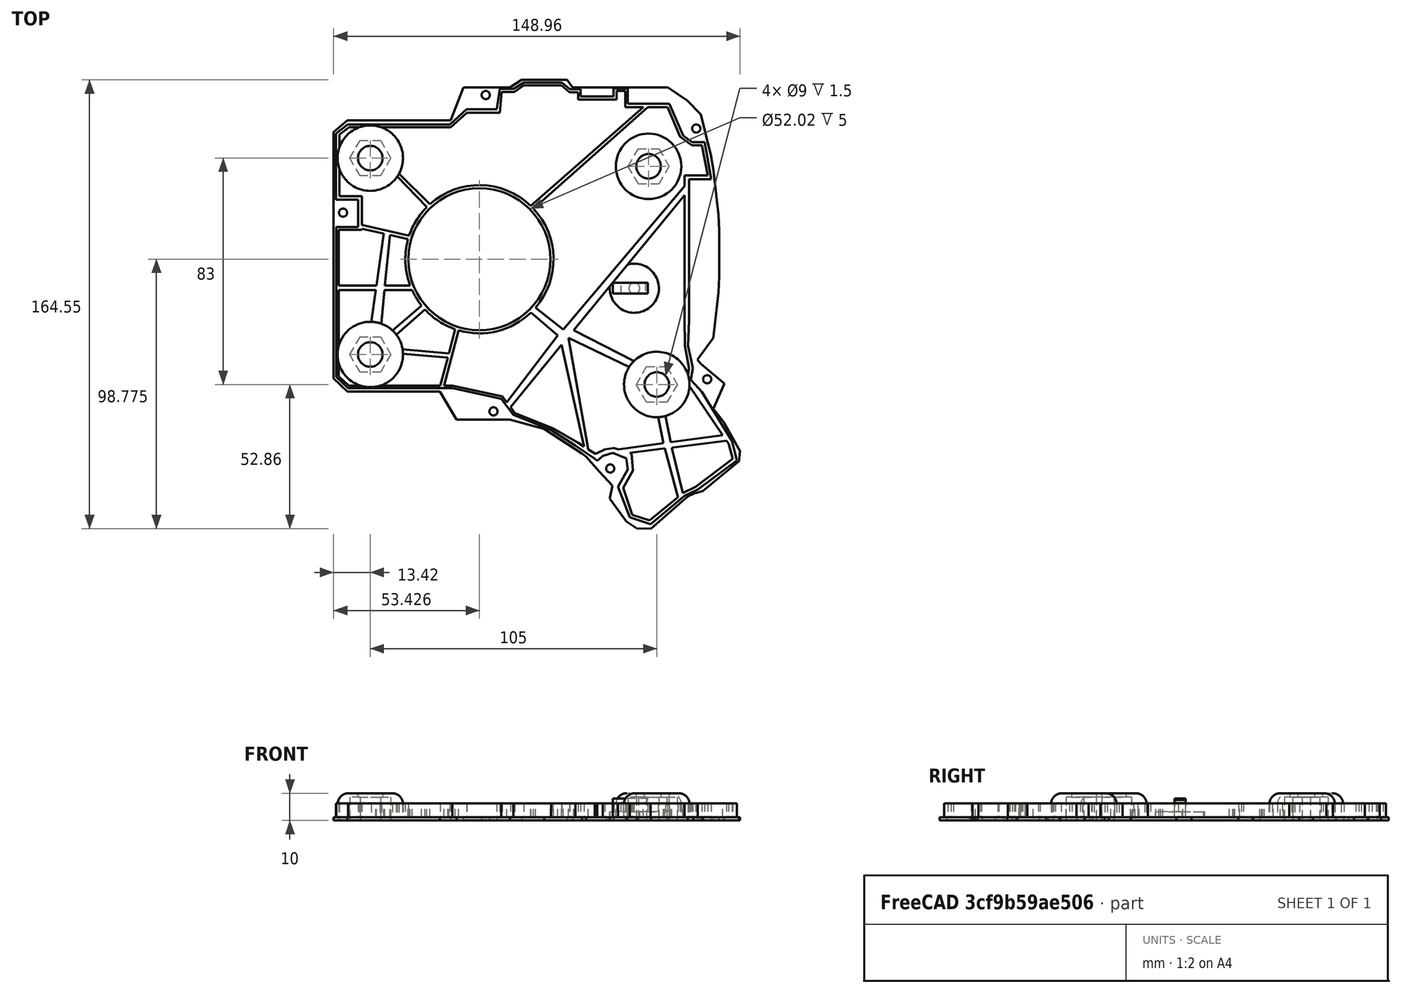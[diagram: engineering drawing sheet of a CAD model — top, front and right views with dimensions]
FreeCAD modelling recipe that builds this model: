
FCSTD DOCUMENT  (FreeCAD 0.19R14555 (Git shallow))
Label: bottom_left
License: All rights reserved
LicenseURL: http://en.wikipedia.org/wiki/All_rights_reserved
objects: Part::Extrusion×13, Sketcher::SketchObject×9, Part::Cut×7, Part::MultiFuse×2, Mesh::Feature×2, Part::Fillet×1, Part::Mirroring×1
note: 33 computed .brp shape members not serialized (recipe doc carries the construction recipe); baked Part::Feature solids carry a one-line shape summary decoded from their .brp

FEATURE [Sketcher::SketchObject] Sketch
  FullyConstrained = false
  Placement = pos=(0,0,0) rot=(1,0,0;1.5708rad)
  sketch-geometry (7):
    g0: LineSegment StartX=-26.8806 StartY=-4.41101 StartZ=0 EndX=-26.8806 EndY=-0.870948 EndZ=0
    g1: LineSegment StartX=-26.8806 StartY=-0.870948 StartZ=0 EndX=-35.8327 EndY=-0.870948 EndZ=0
    g2: LineSegment StartX=-35.8327 StartY=-0.870948 StartZ=0 EndX=-36.775 EndY=0.249898 EndZ=0
    g3: LineSegment StartX=-36.775 StartY=0.249898 StartZ=0 EndX=-36.775 EndY=0.77812 EndZ=0
    g4: LineSegment StartX=-36.775 StartY=0.77812 StartZ=0 EndX=-23.8806 EndY=0.77812 EndZ=0
    g5: LineSegment StartX=-23.8806 StartY=0.77812 StartZ=0 EndX=-23.8806 EndY=-4.41101 EndZ=0
    g6: LineSegment StartX=-23.8806 StartY=-4.41101 StartZ=0 EndX=-26.8806 EndY=-4.41101 EndZ=0
  constraints (14):
    c: Vertical(g0)
    c: Coincident(g0,g1)
    c: Horizontal(g1)
    c: Coincident(g1,g2)
    c: Coincident(g2,g3)
    c: Vertical(g3)
    c: Coincident(g3,g4)
    c: Horizontal(g4)
    c: Coincident(g4,g5)
    c: Vertical(g5)
    c: Coincident(g6,g5)
    c: Coincident(g6,g0)
    c: Horizontal(g6)
    c: Distance(g6) = 3
FEATURE [Part::Extrusion] Extrude  label="Schalterhalter"
  Base = -> Sketch
  Dir = (0,-1,2e-16)
  DirMode = 2
  FaceMakerClass = Part::FaceMakerBullseye
  LengthFwd = 4
  LengthRev = 0
  Placement = pos=(0,-10.7,0) rot=(0,0,1;0rad)
  Solid = true
  Symmetric = false
FEATURE [Sketcher::SketchObject] Sketch031
  FullyConstrained = false
  Placement = pos=(0,0,0) rot=(1,0,0;3.14159rad)
  sketch-geometry (102):
    g0: LineSegment StartX=-24.1385 StartY=-60.4779 StartZ=0 EndX=-29.3451 EndY=-60.4779 EndZ=0
    g1: LineSegment StartX=-29.3451 StartY=-60.4779 StartZ=0 EndX=-29.3451 EndY=-54.9411 EndZ=0
    g2: LineSegment StartX=-29.3451 StartY=-54.9411 StartZ=0 EndX=-44.617 EndY=-54.9411 EndZ=0
    g3: LineSegment StartX=-44.617 StartY=-54.9411 StartZ=0 EndX=-49.6427 EndY=-43.3137 EndZ=0
    g4: LineSegment StartX=-49.6427 StartY=-43.3137 StartZ=0 EndX=-52.9932 EndY=-40.8008 EndZ=0
    g5: LineSegment StartX=-52.9932 StartY=-40.8008 StartZ=0 EndX=-57.5179 EndY=-40.8008 EndZ=0
    g6: LineSegment StartX=-57.5179 StartY=-40.8008 StartZ=0 EndX=-59.9469 EndY=-27.3014 EndZ=0
    g7: LineSegment StartX=-59.9469 StartY=-27.3014 StartZ=0 EndX=-51.7705 EndY=-27.3014 EndZ=0
    g8: LineSegment StartX=-51.7705 StartY=-27.3014 StartZ=0 EndX=-51.7705 EndY=24.5767 EndZ=0
    g9: LineSegment StartX=-51.7705 StartY=24.5767 StartZ=0 EndX=-51.4821 EndY=33.7697 EndZ=0
    g10: LineSegment StartX=-51.4821 StartY=33.7697 StartZ=0 EndX=-53.2529 EndY=41.8955 EndZ=0
    g11: LineSegment StartX=-53.2529 StartY=41.8955 StartZ=0 EndX=-52.4621 EndY=46.2446 EndZ=0
    g12: LineSegment StartX=-52.4621 StartY=46.2446 StartZ=0 EndX=-56.5226 EndY=50.7262 EndZ=0
    g13: LineSegment StartX=-56.5226 StartY=50.7262 StartZ=0 EndX=-67.5901 EndY=68.7223 EndZ=0
    g14: LineSegment StartX=-67.5901 StartY=68.7223 StartZ=0 EndX=-69.3913 EndY=75.8391 EndZ=0
    g15: LineSegment StartX=-69.3913 StartY=75.8391 StartZ=0 EndX=-55.0632 EndY=86.5815 EndZ=0
    g16: LineSegment StartX=-55.0632 StartY=86.5815 StartZ=0 EndX=-50.1429 EndY=88.8659 EndZ=0
    g17: LineSegment StartX=-50.1429 StartY=88.8659 StartZ=0 EndX=-37.7005 EndY=99.2232 EndZ=0
    g18: LineSegment StartX=-37.7005 StartY=99.2232 StartZ=0 EndX=-30.1005 EndY=96.7191 EndZ=0
    g19: LineSegment StartX=-30.1005 StartY=96.7191 StartZ=0 EndX=-25.7646 EndY=85.523 EndZ=0
    g20: LineSegment StartX=-17.2707 StartY=75.2106 StartZ=0 EndX=-10.1077 EndY=70.3434 EndZ=0
    g21: LineSegment StartX=-10.1077 StartY=70.3434 StartZ=0 EndX=-1.25529 EndY=64.7175 EndZ=0
    g22: LineSegment StartX=-1.25529 StartY=64.7175 StartZ=0 EndX=12.6151 EndY=59.0944 EndZ=0
    g23: LineSegment StartX=12.6151 StartY=59.0944 StartZ=0 EndX=16.9593 EndY=53.2146 EndZ=0
    g24: LineSegment StartX=16.9593 StartY=53.2146 StartZ=0 EndX=34.8576 EndY=49.3476 EndZ=0
    g25: LineSegment StartX=34.8576 StartY=49.3476 StartZ=0 EndX=73.1246 EndY=49.3476 EndZ=0
    g26: LineSegment StartX=73.1246 StartY=49.3476 StartZ=0 EndX=77.4982 EndY=45.2021 EndZ=0
    g27: LineSegment StartX=77.4982 StartY=45.2021 StartZ=0 EndX=77.4982 EndY=-9.69727 EndZ=0
    g28: LineSegment StartX=77.4982 StartY=-9.69727 StartZ=0 EndX=69.5024 EndY=-9.69727 EndZ=0
    g29: LineSegment StartX=69.5024 StartY=-9.69727 StartZ=0 EndX=69.5024 EndY=-19.8189 EndZ=0
    g30: LineSegment StartX=69.5024 StartY=-19.8189 StartZ=0 EndX=77.6247 EndY=-19.8189 EndZ=0
    g31: LineSegment StartX=77.6247 StartY=-19.8189 StartZ=0 EndX=77.6247 EndY=-44.0607 EndZ=0
    g32: LineSegment StartX=77.6247 StartY=-44.0607 StartZ=0 EndX=73.2508 EndY=-47.3458 EndZ=0
    g33: LineSegment StartX=73.2508 StartY=-47.3458 StartZ=0 EndX=35.7634 EndY=-47.3458 EndZ=0
    g34: LineSegment StartX=35.7634 StartY=-47.3458 StartZ=0 EndX=29.7437 EndY=-52.8546 EndZ=0
    g35: LineSegment StartX=29.7437 StartY=-52.8546 StartZ=0 EndX=18.6224 EndY=-52.8546 EndZ=0
    g36: LineSegment StartX=18.6224 StartY=-52.8546 StartZ=0 EndX=17.5482 EndY=-60.3492 EndZ=0
    g37: LineSegment StartX=17.5482 StartY=-60.3492 StartZ=0 EndX=12.4995 EndY=-60.3492 EndZ=0
    g38: LineSegment StartX=12.4995 StartY=-60.3492 StartZ=0 EndX=8.72547 EndY=-62.7272 EndZ=0
    g39: LineSegment StartX=8.72547 StartY=-62.7272 StartZ=0 EndX=-5.26983 EndY=-62.7272 EndZ=0
    g40: LineSegment StartX=-5.26983 StartY=-62.7272 StartZ=0 EndX=-8.14386 EndY=-60.228 EndZ=0
    g41: LineSegment StartX=-8.14386 StartY=-60.228 StartZ=0 EndX=-12.0176 EndY=-60.228 EndZ=0
    g42: LineSegment StartX=-12.0176 StartY=-60.228 StartZ=0 EndX=-12.0176 EndY=-57.6039 EndZ=0
    g43: LineSegment StartX=-12.0176 StartY=-57.6039 StartZ=0 EndX=-24.1385 EndY=-57.6039 EndZ=0
    g44: LineSegment StartX=-24.1385 StartY=-57.6039 StartZ=0 EndX=-24.1385 EndY=-60.4779 EndZ=0
    g45: LineSegment StartX=16.9355 StartY=-59.2429 StartZ=0 EndX=12.193 EndY=-59.2429 EndZ=0
    g46: LineSegment StartX=12.193 StartY=-59.2429 StartZ=0 EndX=8.68721 EndY=-61.703 EndZ=0
    g47: LineSegment StartX=8.68721 StartY=-61.703 StartZ=0 EndX=-5.1157 EndY=-61.703 EndZ=0
    g48: LineSegment StartX=-5.1157 StartY=-61.703 StartZ=0 EndX=-8.06111 EndY=-59.199 EndZ=0
    g49: LineSegment StartX=-8.06111 StartY=-59.199 StartZ=0 EndX=-11.1342 EndY=-59.199 EndZ=0
    g50: LineSegment StartX=-11.1342 StartY=-59.199 StartZ=0 EndX=-11.1342 EndY=-56.4281 EndZ=0
    g51: LineSegment StartX=-11.1342 StartY=-56.4281 StartZ=0 EndX=-25.2534 EndY=-56.4281 EndZ=0
    g52: LineSegment StartX=-25.2534 StartY=-56.4281 StartZ=0 EndX=-25.2534 EndY=-59.5911 EndZ=0
    g53: LineSegment StartX=-25.2534 StartY=-59.5911 StartZ=0 EndX=-28.5042 EndY=-59.5911 EndZ=0
    g54: LineSegment StartX=-28.5042 StartY=-59.5911 StartZ=0 EndX=-28.5042 EndY=-53.7043 EndZ=0
    g55: LineSegment StartX=-28.5042 StartY=-53.7043 StartZ=0 EndX=-43.924 EndY=-53.7043 EndZ=0
    g56: LineSegment StartX=-43.924 StartY=-53.7043 StartZ=0 EndX=-48.5049 EndY=-42.8877 EndZ=0
    g57: LineSegment StartX=-48.5049 StartY=-42.8877 StartZ=0 EndX=-52.8786 EndY=-39.7686 EndZ=0
    g58: LineSegment StartX=-52.8786 StartY=-39.7686 StartZ=0 EndX=-56.5882 EndY=-39.7686 EndZ=0
    g59: LineSegment StartX=-56.5882 StartY=-39.7686 StartZ=0 EndX=-58.6529 EndY=-28.6102 EndZ=0
    g60: LineSegment StartX=-58.6529 StartY=-28.6102 StartZ=0 EndX=-50.1741 EndY=-28.6102 EndZ=0
    g61: LineSegment StartX=-50.1741 StartY=-28.6102 StartZ=0 EndX=-50.1741 EndY=23.5651 EndZ=0
    g62: LineSegment StartX=-50.1741 StartY=23.5651 StartZ=0 EndX=-50.3095 EndY=33.8562 EndZ=0
    g63: LineSegment StartX=-50.3095 StartY=33.8562 StartZ=0 EndX=-51.8031 EndY=42.0273 EndZ=0
    g64: LineSegment StartX=-51.8031 StartY=42.0273 StartZ=0 EndX=-50.9245 EndY=46.9475 EndZ=0
    g65: LineSegment StartX=-50.9245 StartY=46.9475 StartZ=0 EndX=-66.2722 EndY=69.6888 EndZ=0
    g66: LineSegment StartX=-66.2722 StartY=69.6888 StartZ=0 EndX=-67.8031 EndY=75.2474 EndZ=0
    g67: LineSegment StartX=-67.8031 StartY=75.2474 StartZ=0 EndX=-54.2724 EndY=85.4832 EndZ=0
    g68: LineSegment StartX=-54.2724 StartY=85.4832 StartZ=0 EndX=-49.5718 EndY=87.8555 EndZ=0
    g69: LineSegment StartX=-49.5718 StartY=87.8555 StartZ=0 EndX=-37.403 EndY=97.7838 EndZ=0
    g70: LineSegment StartX=-37.403 StartY=97.7838 StartZ=0 EndX=-30.9452 EndY=95.8509 EndZ=0
    g71: LineSegment StartX=-30.9452 StartY=95.8509 StartZ=0 EndX=-27.7256 EndY=85.9358 EndZ=0
    g72: LineSegment StartX=-17.5596 StartY=73.4993 StartZ=0 EndX=-11.2059 EndY=69.3769 EndZ=0
    g73: LineSegment StartX=-11.2059 StartY=69.3769 StartZ=0 EndX=-1.89314 EndY=64.0587 EndZ=0
    g74: LineSegment StartX=-1.89314 StartY=64.0587 StartZ=0 EndX=12.006 EndY=58.4019 EndZ=0
    g75: LineSegment StartX=12.006 StartY=58.4019 StartZ=0 EndX=16.5662 EndY=52.3162 EndZ=0
    g76: LineSegment StartX=16.5662 StartY=52.3162 StartZ=0 EndX=34.9016 EndY=48.4585 EndZ=0
    g77: LineSegment StartX=34.9016 StartY=48.4585 StartZ=0 EndX=72.868 EndY=48.4585 EndZ=0
    g78: LineSegment StartX=72.868 StartY=48.4585 StartZ=0 EndX=76.5288 EndY=44.9389 EndZ=0
    g79: LineSegment StartX=76.5288 StartY=44.9389 StartZ=0 EndX=76.5288 EndY=-8.70233 EndZ=0
    g80: LineSegment StartX=76.5288 StartY=-8.70233 StartZ=0 EndX=68.0803 EndY=-8.70233 EndZ=0
    g81: LineSegment StartX=68.0803 StartY=-8.70233 StartZ=0 EndX=68.0803 EndY=-21.0197 EndZ=0
    g82: LineSegment StartX=68.0803 StartY=-21.0197 StartZ=0 EndX=76.3385 EndY=-21.0197 EndZ=0
    g83: LineSegment StartX=76.3385 StartY=-21.0197 StartZ=0 EndX=76.3385 EndY=-43.5888 EndZ=0
    g84: LineSegment StartX=76.3385 StartY=-43.5888 StartZ=0 EndX=72.8241 EndY=-46.2686 EndZ=0
    g85: LineSegment StartX=72.8241 StartY=-46.2686 StartZ=0 EndX=35.499 EndY=-46.2686 EndZ=0
    g86: LineSegment StartX=35.499 StartY=-46.2686 StartZ=0 EndX=29.59 EndY=-51.5989 EndZ=0
    g87: LineSegment StartX=29.59 StartY=-51.5989 StartZ=0 EndX=17.5526 EndY=-51.5989 EndZ=0
    g88: LineSegment StartX=17.5526 StartY=-51.5989 StartZ=0 EndX=16.9355 EndY=-59.2429 EndZ=0
    g89: Circle CenterX=24.994 CenterY=2.08531 CenterZ=0 NormalX=0 NormalY=0 NormalZ=1 AngleXU=0 Radius=26.0078
    g90: Circle CenterX=24.994 CenterY=2.08531 CenterZ=0 NormalX=0 NormalY=0 NormalZ=1 AngleXU=0 Radius=27.1592
    g91: LineSegment StartX=-25.7646 StartY=85.523 StartZ=0 EndX=-29.3769 EndY=79.1757 EndZ=0
    g92: LineSegment StartX=-29.3769 StartY=79.1757 StartZ=0 EndX=-28.8093 EndY=75.1506 EndZ=0
    g93: LineSegment StartX=-28.8093 StartY=75.1506 StartZ=0 EndX=-23.9069 EndY=73.0348 EndZ=0
    g94: LineSegment StartX=-23.9069 StartY=73.0348 StartZ=0 EndX=-20.1398 EndY=74.2217 EndZ=0
    g95: LineSegment StartX=-20.1398 StartY=74.2217 StartZ=0 EndX=-18.2305 EndY=75.9247 EndZ=0
    g96: LineSegment StartX=-18.2305 StartY=75.9247 StartZ=0 EndX=-17.2707 EndY=75.2106 EndZ=0
    g97: LineSegment StartX=-17.5596 StartY=73.4993 StartZ=0 EndX=-20.9655 EndY=71.7963 EndZ=0
    g98: LineSegment StartX=-20.9655 StartY=71.7963 StartZ=0 EndX=-24.2165 EndY=71.2287 EndZ=0
    g99: LineSegment StartX=-24.2165 StartY=71.2287 StartZ=0 EndX=-30.7702 EndY=73.2412 EndZ=0
    g100: LineSegment StartX=-30.7702 StartY=73.2412 StartZ=0 EndX=-31.2863 EndY=79.5369 EndZ=0
    g101: LineSegment StartX=-31.2863 StartY=79.5369 StartZ=0 EndX=-27.7256 EndY=85.9358 EndZ=0
  constraints (141):
    c: Horizontal(g0)
    c: Coincident(g0,g1)
    c: Vertical(g1)
    c: Coincident(g1,g2)
    c: Horizontal(g2)
    c: Coincident(g2,g3)
    c: Coincident(g3,g4)
    c: Coincident(g4,g5)
    c: Horizontal(g5)
    c: Coincident(g5,g6)
    c: Coincident(g6,g7)
    c: Horizontal(g7)
    c: Coincident(g7,g8)
    c: Vertical(g8)
    c: Coincident(g8,g9)
    c: Coincident(g9,g10)
    c: Coincident(g10,g11)
    c: Coincident(g11,g12)
    c: Coincident(g12,g13)
    c: Coincident(g13,g14)
    c: Coincident(g14,g15)
    c: Coincident(g15,g16)
    c: Coincident(g16,g17)
    c: Coincident(g17,g18)
    c: Coincident(g18,g19)
    c: Coincident(g20,g21)
    c: Coincident(g21,g22)
    c: Coincident(g22,g23)
    c: Coincident(g23,g24)
    c: Coincident(g24,g25)
    c: Horizontal(g25)
    c: Coincident(g25,g26)
    c: Coincident(g26,g27)
    c: Vertical(g27)
    c: Coincident(g27,g28)
    c: Horizontal(g28)
    c: Coincident(g28,g29)
    c: Vertical(g29)
    c: Coincident(g29,g30)
    c: Horizontal(g30)
    c: Coincident(g30,g31)
    c: Vertical(g31)
    c: Coincident(g31,g32)
    c: Coincident(g32,g33)
    c: Horizontal(g33)
    c: Coincident(g33,g34)
    c: Coincident(g34,g35)
    c: Horizontal(g35)
    c: Coincident(g35,g36)
    c: Coincident(g36,g37)
    c: Horizontal(g37)
    c: Coincident(g37,g38)
    c: Coincident(g38,g39)
    c: Horizontal(g39)
    c: Coincident(g39,g40)
    c: Coincident(g40,g41)
    c: Horizontal(g41)
    c: Coincident(g41,g42)
    c: Vertical(g42)
    c: Coincident(g42,g43)
    c: Horizontal(g43)
    c: Coincident(g43,g44)
    c: Coincident(g44,g0)
    c: Vertical(g44)
    c: Horizontal(g45)
    c: Coincident(g45,g46)
    c: Coincident(g46,g47)
    c: Horizontal(g47)
    c: Coincident(g47,g48)
    c: Coincident(g48,g49)
    c: Horizontal(g49)
    c: Coincident(g49,g50)
    c: Vertical(g50)
    c: Coincident(g50,g51)
    c: Horizontal(g51)
    c: Coincident(g51,g52)
    c: Vertical(g52)
    c: Coincident(g52,g53)
    c: Horizontal(g53)
    c: Coincident(g53,g54)
    c: Vertical(g54)
    c: Coincident(g54,g55)
    c: Horizontal(g55)
    c: Coincident(g55,g56)
    c: Coincident(g56,g57)
    c: Coincident(g57,g58)
    c: Horizontal(g58)
    c: Coincident(g58,g59)
    c: Coincident(g59,g60)
    c: Horizontal(g60)
    c: Coincident(g60,g61)
    c: Vertical(g61)
    c: Coincident(g61,g62)
    c: Coincident(g62,g63)
    c: Coincident(g63,g64)
    c: Coincident(g64,g65)
    c: Coincident(g65,g66)
    c: Coincident(g66,g67)
    c: Coincident(g67,g68)
    c: Coincident(g68,g69)
    c: Coincident(g69,g70)
    c: Coincident(g70,g71)
    c: Coincident(g72,g73)
    c: Coincident(g73,g74)
    c: Coincident(g74,g75)
    c: Coincident(g75,g76)
    c: Coincident(g76,g77)
    c: Horizontal(g77)
    c: Coincident(g77,g78)
    c: Coincident(g78,g79)
    c: Vertical(g79)
    c: Coincident(g79,g80)
    c: Horizontal(g80)
    c: Coincident(g80,g81)
    c: Vertical(g81)
    c: Coincident(g81,g82)
    c: Horizontal(g82)
    c: Coincident(g82,g83)
    c: Vertical(g83)
    c: Coincident(g83,g84)
    c: Coincident(g84,g85)
    c: Horizontal(g85)
    c: Coincident(g85,g86)
    c: Coincident(g86,g87)
    c: Horizontal(g87)
    c: Coincident(g87,g88)
    c: Coincident(g88,g45)
    c: Coincident(g90,g89)
    c: Coincident(g91,g19)
    c: Coincident(g92,g91)
    c: Coincident(g93,g92)
    c: Coincident(g94,g93)
    c: Coincident(g95,g94)
    c: Coincident(g96,g95)
    c: Coincident(g96,g20)
    c: Coincident(g97,g72)
    c: Coincident(g98,g97)
    c: Coincident(g99,g98)
    c: Coincident(g100,g99)
    c: Coincident(g101,g100)
    c: Coincident(g101,g71)
FEATURE [Part::Extrusion] Extrude026
  Base = -> Sketch031
  Dir = (0,0,-1)
  DirMode = 2
  FaceMakerClass = Part::FaceMakerBullseye
  LengthFwd = 5
  LengthRev = 0
  Placement = pos=(0,0,-1) rot=(0,0,1;0rad)
  Solid = true
  Symmetric = false
FEATURE [Sketcher::SketchObject] Sketch032
  FullyConstrained = false
  sketch-geometry (63):
    g0: LineSegment StartX=-32.5769 StartY=-39.9295 StartZ=0 EndX=-9.54298 EndY=-28.1078 EndZ=0
    g1: LineSegment StartX=-30.7152 StartY=-41.9456 StartZ=0 EndX=-32.5769 EndY=-39.9295 EndZ=0
    g2: LineSegment StartX=32.5107 StartY=-27.5505 StartZ=0 EndX=38.0602 EndY=-48.9351 EndZ=0
    g3: LineSegment StartX=38.0602 StartY=-48.9351 StartZ=0 EndX=39.3736 EndY=-48.6733 EndZ=0
    g4: LineSegment StartX=39.3736 StartY=-48.6733 StartZ=0 EndX=36.6148 EndY=-38.1783 EndZ=0
    g5: LineSegment StartX=33.7238 StartY=-27.1808 StartZ=0 EndX=32.5107 EndY=-27.5505 EndZ=0
    g6: LineSegment StartX=50.4968 StartY=5.20014 StartZ=0 EndX=57.8214 EndY=6.84598 EndZ=0
    g7: LineSegment StartX=69.1965 StartY=9.40202 StartZ=0 EndX=69.1965 EndY=10.7361 EndZ=0
    g8: LineSegment StartX=69.1965 StartY=10.7361 StartZ=0 EndX=49.9077 EndY=6.36256 EndZ=0
    g9: LineSegment StartX=49.9077 StartY=6.36256 StartZ=0 EndX=50.4968 EndY=5.20014 EndZ=0
    g10: LineSegment StartX=6.85712 StartY=16.9685 StartZ=0 EndX=-36.1659 EndY=54.6592 EndZ=0
    g11: LineSegment StartX=-36.1659 StartY=54.6592 StartZ=0 EndX=-37.7589 EndY=54.5817 EndZ=0
    g12: LineSegment StartX=-37.7589 StartY=54.5817 StartZ=0 EndX=5.83785 EndY=15.8428 EndZ=0
    g13: LineSegment StartX=5.83785 StartY=15.8428 StartZ=0 EndX=6.85712 EndY=16.9685 EndZ=0
    g14: LineSegment StartX=-30.7152 StartY=-41.9456 StartZ=0 EndX=-7.65656 EndY=-30.8878 EndZ=0
    g15: LineSegment StartX=-15.0169 StartY=-72.5869 StartZ=0 EndX=-13.4959 EndY=-71.5729 EndZ=0
    g16: LineSegment StartX=-13.4959 StartY=-71.5729 StartZ=0 EndX=-5.11632 EndY=-33.503 EndZ=0
    g17: LineSegment StartX=44.4369 StartY=-20.0606 StartZ=0 EndX=56.2289 EndY=-30.3786 EndZ=0
    g18: LineSegment StartX=56.2289 StartY=-30.3786 StartZ=0 EndX=57.3297 EndY=-28.5909 EndZ=0
    g19: LineSegment StartX=57.3297 StartY=-28.5909 StartZ=0 EndX=45.6345 EndY=-18.5823 EndZ=0
    g20: LineSegment StartX=45.6345 StartY=-18.5823 StartZ=0 EndX=44.4369 EndY=-20.0606 EndZ=0
    g21: LineSegment StartX=55.0145 StartY=29.918 StartZ=0 EndX=42.7023 EndY=17.6926 EndZ=0
    g22: LineSegment StartX=42.7023 StartY=17.6926 StartZ=0 EndX=43.6798 EndY=16.4587 EndZ=0
    g23: LineSegment StartX=43.6798 StartY=16.4587 StartZ=0 EndX=55.8612 EndY=29.0011 EndZ=0
    g24: LineSegment StartX=55.8612 StartY=29.0011 StartZ=0 EndX=55.0145 EndY=29.918 EndZ=0
    g25: LineSegment StartX=36.2165 StartY=-36.6632 StartZ=0 EndX=53.7558 EndY=-34.9819 EndZ=0
    g26: LineSegment StartX=53.7558 StartY=-34.9819 StartZ=0 EndX=53.3152 EndY=-36.7098 EndZ=0
    g27: LineSegment StartX=53.3152 StartY=-36.7098 StartZ=0 EndX=36.6148 EndY=-38.1783 EndZ=0
    g28: LineSegment StartX=36.2165 StartY=-36.6632 StartZ=0 EndX=33.7238 EndY=-27.1808 EndZ=0
    g29: LineSegment StartX=57.8214 StartY=6.84598 StartZ=0 EndX=59.6195 EndY=-11.7601 EndZ=0
    g30: LineSegment StartX=60.9963 StartY=-26.0063 StartZ=0 EndX=64.7176 EndY=-25.5862 EndZ=0
    g31: LineSegment StartX=64.7176 StartY=-25.5862 StartZ=0 EndX=62.9989 EndY=-13.4017 EndZ=0
    g32: LineSegment StartX=60.0714 StartY=7.35159 StartZ=0 EndX=69.1965 EndY=9.40202 EndZ=0
    g33: LineSegment StartX=-49.6869 StartY=-88.2689 StartZ=0 EndX=-47.9566 EndY=-89.9327 EndZ=0
    g34: LineSegment StartX=-47.9566 StartY=-89.9327 StartZ=0 EndX=-42.9299 EndY=-71.4391 EndZ=0
    g35: LineSegment StartX=62.7673 StartY=-11.7601 StartZ=0 EndX=77.2056 EndY=-11.7601 EndZ=0
    g36: LineSegment StartX=77.2056 StartY=-11.7601 StartZ=0 EndX=77.2056 EndY=-13.4017 EndZ=0
    g37: LineSegment StartX=77.2056 StartY=-13.4017 StartZ=0 EndX=62.9989 EndY=-13.4017 EndZ=0
    g38: LineSegment StartX=59.7782 StartY=-13.4017 StartZ=0 EndX=48.6753 EndY=-13.4017 EndZ=0
    g39: LineSegment StartX=48.6753 StartY=-13.4017 StartZ=0 EndX=49.3718 EndY=-11.7601 EndZ=0
    g40: LineSegment StartX=49.3718 StartY=-11.7601 StartZ=0 EndX=59.6195 EndY=-11.7601 EndZ=0
    g41: LineSegment StartX=59.7782 StartY=-13.4017 StartZ=0 EndX=60.9963 EndY=-26.0063 EndZ=0
    g42: LineSegment StartX=62.7673 StartY=-11.7601 StartZ=0 EndX=60.0714 EndY=7.35159 EndZ=0
    g43: LineSegment StartX=-65.0366 StartY=-66.5004 StartZ=0 EndX=-66.1967 EndY=-68.5189 EndZ=0
    g44: LineSegment StartX=-66.1967 StartY=-68.5189 StartZ=0 EndX=-45.4188 EndY=-71.1267 EndZ=0
    g45: LineSegment StartX=-25.7061 StartY=-73.6009 StartZ=0 EndX=-24.4808 EndY=-71.9531 EndZ=0
    g46: LineSegment StartX=-24.4808 StartY=-71.9531 StartZ=0 EndX=-42.4246 EndY=-69.5406 EndZ=0
    g47: LineSegment StartX=-45.4188 StartY=-71.1267 StartZ=0 EndX=-49.6869 EndY=-88.2689 EndZ=0
    g48: LineSegment StartX=-42.9299 StartY=-71.4391 StartZ=0 EndX=-25.7061 EndY=-73.6009 EndZ=0
    g49: LineSegment StartX=13.9098 StartY=-56.6917 StartZ=0 EndX=-5.11632 EndY=-33.503 EndZ=0
    g50: LineSegment StartX=-51.0941 StartY=22.5342 StartZ=0 EndX=-51.0941 EndY=25.8134 EndZ=0
    g51: LineSegment StartX=-51.0941 StartY=25.8134 StartZ=0 EndX=-5.73278 EndY=-27.8323 EndZ=0
    g52: LineSegment StartX=15.1277 StartY=-54.8099 StartZ=0 EndX=13.9098 EndY=-56.6917 EndZ=0
    g53: LineSegment StartX=-7.65656 StartY=-30.8878 StartZ=0 EndX=-15.0169 EndY=-72.5869 EndZ=0
    g54: LineSegment StartX=-9.54298 StartY=-28.1078 StartZ=0 EndX=-51.0941 EndY=22.5342 EndZ=0
    g55: LineSegment StartX=-3.74708 StartY=-30.0166 StartZ=0 EndX=15.1277 EndY=-54.8099 EndZ=0
    g56: LineSegment StartX=-5.73278 StartY=-27.8323 StartZ=0 EndX=4.80151 EndY=-19.6249 EndZ=0
    g57: LineSegment StartX=4.80151 StartY=-19.6249 StartZ=0 EndX=6.47927 EndY=-21.2795 EndZ=0
    g58: LineSegment StartX=6.47927 StartY=-21.2795 StartZ=0 EndX=-3.74708 EndY=-30.0166 EndZ=0
    g59: LineSegment StartX=-45.0759 StartY=-69.1841 StartZ=0 EndX=-42.9979 EndY=-58.5171 EndZ=0
    g60: LineSegment StartX=-42.9979 StartY=-58.5171 StartZ=0 EndX=-40.2766 EndY=-58.8293 EndZ=0
    g61: LineSegment StartX=-40.2766 StartY=-58.8293 StartZ=0 EndX=-42.4246 EndY=-69.5406 EndZ=0
    g62: LineSegment StartX=-45.0759 StartY=-69.1841 StartZ=0 EndX=-65.0366 EndY=-66.5004 EndZ=0
  constraints (78):
    c: Coincident(g1,g0)
    c: Coincident(g2,g3)
    c: Coincident(g3,g4)
    c: Coincident(g28,g5)
    c: Coincident(g5,g2)
    c: Coincident(g32,g7)
    c: Vertical(g7)
    c: Coincident(g7,g8)
    c: Coincident(g8,g9)
    c: Coincident(g9,g6)
    c: Coincident(g11,g12)
    c: Coincident(g12,g13)
    c: Coincident(g13,g10)
    c: Coincident(g53,g15)
    c: Coincident(g15,g16)
    c: Coincident(g17,g18)
    c: Coincident(g18,g19)
    c: Coincident(g19,g20)
    c: Coincident(g20,g17)
    c: Coincident(g21,g22)
    c: Coincident(g22,g23)
    c: Coincident(g23,g24)
    c: Coincident(g24,g21)
    c: Coincident(g26,g25)
    c: Coincident(g4,g27)
    c: Coincident(g28,g25)
    c: Tangent(g4,g28)
    c: Coincident(g41,g30)
    c: Coincident(g30,g31)
    c: Coincident(g6,g29)
    c: Coincident(g32,g42)
    c: Tangent(g6,g32)
    c: Coincident(g47,g33)
    c: Coincident(g33,g34)
    c: Horizontal(g35)
    c: Coincident(g35,g36)
    c: Vertical(g36)
    c: Coincident(g36,g37)
    c: Horizontal(g37)
    c: Horizontal(g38)
    c: Coincident(g38,g39)
    c: Coincident(g39,g40)
    c: Horizontal(g40)
    c: Coincident(g29,g40)
    c: Coincident(g41,g38)
    c: Tangent(g29,g41)
    c: Coincident(g31,g37)
    c: Coincident(g42,g35)
    c: Tangent(g31,g42)
    c: PointOnObject(g31,g38)
    c: PointOnObject(g35,g40)
    c: Coincident(g10,g11)
    c: Coincident(g43,g44)
    c: Coincident(g48,g45)
    c: Coincident(g45,g46)
    c: Coincident(g44,g47)
    c: Coincident(g48,g34)
    c: Tangent(g44,g48)
    c: Coincident(g43,g62)
    c: Coincident(g14,g1)
    c: Coincident(g54,g50)
    c: Vertical(g50)
    c: Coincident(g50,g51)
    c: Coincident(g55,g52)
    c: Coincident(g52,g49)
    c: Coincident(g54,g0)
    c: Tangent(g49,g54)
    c: Coincident(g49,g16)
    c: Coincident(g14,g53)
    c: Coincident(g51,g56)
    c: Coincident(g56,g57)
    c: Coincident(g57,g58)
    c: Coincident(g58,g55)
    c: Coincident(g59,g60)
    c: Coincident(g60,g61)
    c: Coincident(g46,g61)
    c: Coincident(g62,g59)
    c: Tangent(g46,g62)
FEATURE [Part::Extrusion] Extrude028  label="Querstreben"
  Base = -> Sketch032
  Dir = (0,0,1)
  DirMode = 2
  FaceMakerClass = Part::FaceMakerBullseye
  LengthFwd = 5
  LengthRev = 0
  Placement = pos=(0,0,-6) rot=(0,0,1;0rad)
  Solid = true
  Symmetric = false
FEATURE [Sketcher::SketchObject] Sketch054
  FullyConstrained = false
  Placement = pos=(0,0,-4) rot=(1,0,0;3.14159rad)
  sketch-geometry (42):
    g0: LineSegment StartX=-44.1096 StartY=-60.8699 StartZ=0 EndX=-51.1597 EndY=-56.0764 EndZ=0
    g1: LineSegment StartX=-51.1597 StartY=-56.0764 StartZ=0 EndX=-56.1597 EndY=-51.0764 EndZ=0
    g2: LineSegment StartX=-56.1597 StartY=-51.0764 StartZ=0 EndX=-59.8373 EndY=-36.0023 EndZ=0
    g3: LineSegment StartX=-59.8373 StartY=-36.0023 StartZ=0 EndX=-60.7273 EndY=-30.9176 EndZ=0
    g4: LineSegment StartX=-60.7273 StartY=-30.9176 StartZ=0 EndX=-62.6338 EndY=-14.0857 EndZ=0
    g5: LineSegment StartX=-62.6338 StartY=-14.0857 StartZ=0 EndX=-62.9339 EndY=-8.65493 EndZ=0
    g6: LineSegment StartX=-62.9339 StartY=-8.65493 StartZ=0 EndX=-62.9339 EndY=8.50371 EndZ=0
    g7: LineSegment StartX=-62.9339 StartY=8.50371 StartZ=0 EndX=-62.6306 EndY=14.1113 EndZ=0
    g8: LineSegment StartX=-62.6306 StartY=14.1113 StartZ=0 EndX=-60.7274 EndY=30.9184 EndZ=0
    g9: LineSegment StartX=-60.7274 StartY=30.9184 StartZ=0 EndX=-54.9343 EndY=38.937 EndZ=0
    g10: LineSegment StartX=-54.9343 StartY=38.937 StartZ=0 EndX=-56.1902 EndY=40.4684 EndZ=0
    g11: LineSegment StartX=-64.8157 StartY=47.7061 StartZ=0 EndX=-60.7702 EndY=56.9561 EndZ=0
    g12: LineSegment StartX=-60.7702 StartY=56.9561 StartZ=0 EndX=-64.4792 EndY=61.7033 EndZ=0
    g13: LineSegment StartX=-64.4792 StartY=61.7033 StartZ=0 EndX=-70.5416 EndY=72.3745 EndZ=0
    g14: LineSegment StartX=-70.5416 StartY=72.3745 StartZ=0 EndX=-70.1745 EndY=76.1634 EndZ=0
    g15: LineSegment StartX=-70.1745 StartY=76.1634 StartZ=0 EndX=-56.8443 EndY=87.0814 EndZ=0
    g16: LineSegment StartX=-51.3142 StartY=89.1273 StartZ=0 EndX=-37.9034 EndY=100.86 EndZ=0
    g17: LineSegment StartX=-23.7658 StartY=85.1928 StartZ=0 EndX=-18.9923 EndY=79.8913 EndZ=0
    g18: LineSegment StartX=-18.9923 StartY=79.8913 StartZ=0 EndX=-14.1134 EndY=74.4727 EndZ=0
    g19: LineSegment StartX=1.2105 StartY=64.3357 StartZ=0 EndX=13.8377 EndY=60.8699 EndZ=0
    g20: LineSegment StartX=13.8377 StartY=60.8699 StartZ=0 EndX=33.3369 EndY=60.8699 EndZ=0
    g21: LineSegment StartX=33.3369 StartY=60.8699 StartZ=0 EndX=39.4269 EndY=50.5485 EndZ=0
    g22: LineSegment StartX=39.4269 StartY=50.5485 StartZ=0 EndX=73.4211 EndY=50.5485 EndZ=0
    g23: LineSegment StartX=73.4211 StartY=50.5485 StartZ=0 EndX=78.4211 EndY=45.7188 EndZ=0
    g24: LineSegment StartX=78.4211 StartY=45.7188 StartZ=0 EndX=78.4211 EndY=-44.5398 EndZ=0
    g25: LineSegment StartX=78.4211 StartY=-44.5398 StartZ=0 EndX=73.4211 EndY=-48.8699 EndZ=0
    g26: LineSegment StartX=73.4211 StartY=-48.8699 StartZ=0 EndX=35.5981 EndY=-48.8699 EndZ=0
    g27: LineSegment StartX=35.5981 StartY=-48.8699 StartZ=0 EndX=30.8749 EndY=-60.8699 EndZ=0
    g28: LineSegment StartX=30.8749 StartY=-60.8699 StartZ=0 EndX=13.8377 EndY=-60.8699 EndZ=0
    g29: LineSegment StartX=13.8377 StartY=-60.8699 StartZ=0 EndX=9.45978 EndY=-63.6899 EndZ=0
    g30: LineSegment StartX=9.45978 StartY=-63.6899 StartZ=0 EndX=-7.15413 EndY=-63.6899 EndZ=0
    g31: LineSegment StartX=-7.15413 StartY=-63.6899 StartZ=0 EndX=-9.13059 EndY=-60.8699 EndZ=0
    g32: LineSegment StartX=-9.13059 StartY=-60.8699 StartZ=0 EndX=-44.1096 EndY=-60.8699 EndZ=0
    g33: LineSegment StartX=-56.1902 StartY=40.4684 StartZ=0 EndX=-64.8157 EndY=47.7061 EndZ=0
    g34: LineSegment StartX=-56.8443 StartY=87.0814 StartZ=0 EndX=-53.5266 EndY=88.046 EndZ=0
    g35: LineSegment StartX=-53.5266 StartY=88.046 StartZ=0 EndX=-51.3142 EndY=89.1273 EndZ=0
    g36: LineSegment StartX=-28.7993 StartY=98.2142 StartZ=0 EndX=-22.7532 EndY=89.8924 EndZ=0
    g37: LineSegment StartX=-22.7532 StartY=89.8924 StartZ=0 EndX=-23.7658 EndY=85.1928 EndZ=0
    g38: LineSegment StartX=-37.9034 StartY=100.86 StartZ=0 EndX=-32.6869 EndY=100.79 EndZ=0
    g39: LineSegment StartX=-32.6869 StartY=100.79 StartZ=0 EndX=-28.7993 EndY=98.2142 EndZ=0
    g40: LineSegment StartX=-14.1134 StartY=74.4727 StartZ=0 EndX=-12.5391 EndY=73.271 EndZ=0
    g41: LineSegment StartX=-12.5391 StartY=73.271 StartZ=0 EndX=1.2105 EndY=64.3357 EndZ=0
  constraints (50):
    c: Coincident(g0,g1)
    c: Coincident(g1,g2)
    c: Coincident(g2,g3)
    c: Coincident(g3,g4)
    c: Coincident(g4,g5)
    c: Coincident(g5,g6)
    c: Vertical(g6)
    c: Coincident(g6,g7)
    c: Coincident(g7,g8)
    c: Coincident(g8,g9)
    c: Coincident(g9,g10)
    c: Coincident(g11,g12)
    c: Coincident(g12,g13)
    c: Coincident(g13,g14)
    c: Coincident(g14,g15)
    c: Coincident(g17,g18)
    c: Coincident(g19,g20)
    c: Horizontal(g20)
    c: Coincident(g20,g21)
    c: Coincident(g21,g22)
    c: Horizontal(g22)
    c: Coincident(g22,g23)
    c: Coincident(g23,g24)
    c: Vertical(g24)
    c: Coincident(g24,g25)
    c: Coincident(g25,g26)
    c: Horizontal(g26)
    c: Coincident(g26,g27)
    c: Coincident(g27,g28)
    c: Horizontal(g28)
    c: Coincident(g28,g29)
    c: Coincident(g29,g30)
    c: Horizontal(g30)
    c: Coincident(g30,g31)
    c: Coincident(g31,g32)
    c: Horizontal(g32)
    c: Coincident(g0,g32)
    c: Coincident(g33,g11)
    c: Coincident(g34,g15)
    c: Coincident(g35,g34)
    c: Coincident(g35,g16)
    c: Coincident(g37,g36)
    c: Coincident(g37,g17)
    c: Coincident(g10,g33)
    c: Coincident(g16,g38)
    c: Coincident(g38,g39)
    c: Coincident(g39,g36)
    c: Coincident(g40,g18)
    c: Coincident(g41,g40)
    c: Coincident(g41,g19)
FEATURE [Part::Extrusion] Extrude044  label="Grund"
  Base = -> Sketch054
  Dir = (0,0,-1)
  DirMode = 2
  FaceMakerClass = Part::FaceMakerBullseye
  LengthFwd = 1.25
  LengthRev = 0
  Placement = pos=(0,0,-2) rot=(0,0,1;0rad)
  Solid = true
  Symmetric = false
FEATURE [Sketcher::SketchObject] Sketch002
  FullyConstrained = false
  sketch-geometry (7):
    g0: LineSegment StartX=3.75278 StartY=6.5 StartZ=0 EndX=-3.75278 EndY=6.5 EndZ=0
    g1: LineSegment StartX=-3.75278 StartY=6.5 StartZ=0 EndX=-7.50555 EndY=-1.2284e-12 EndZ=0
    g2: LineSegment StartX=-7.50555 StartY=-1.2284e-12 StartZ=0 EndX=-3.75278 EndY=-6.5 EndZ=0
    g3: LineSegment StartX=-3.75278 StartY=-6.5 StartZ=0 EndX=3.75278 EndY=-6.5 EndZ=0
    g4: LineSegment StartX=3.75278 StartY=-6.5 StartZ=0 EndX=7.50555 EndY=6.422e-13 EndZ=0
    g5: LineSegment StartX=7.50555 StartY=6.419e-13 StartZ=0 EndX=3.75278 EndY=6.5 EndZ=0
    g6: Circle CenterX=0 CenterY=0 CenterZ=0 NormalX=0 NormalY=0 NormalZ=1 AngleXU=0 Radius=7.50555
  constraints (16):
    c: Coincident(g0,g1)
    c: Coincident(g1,g2)
    c: Coincident(g2,g3)
    c: Coincident(g3,g4)
    c: Coincident(g4,g5)
    c: Coincident(g5,g0)
    c: Equal(g0, g1-g5) x5
    c: PointOnObject(g0,g6)
    c: PointOnObject(g1,g6)
    c: PointOnObject(g2,g6)
    c: PointOnObject(g3,g6)
    c: PointOnObject(g4,g6)
    c: PointOnObject(g5,g6)
    c: Horizontal(g0)
    c: Distance(g3,g1) = 13
    c: Coincident(g6,g-1)
FEATURE [Part::Extrusion] Extrude002  label="Mutterloch"
  Base = -> Sketch002
  Dir = (0,0,1)
  DirMode = 2
  FaceMakerClass = Part::FaceMakerBullseye
  LengthFwd = 8.5
  LengthRev = 0
  Reversed = true
  Solid = true
  Symmetric = false
FEATURE [Sketcher::SketchObject] Sketch055
  FullyConstrained = false
  sketch-geometry (1):
    g0: Circle CenterX=0 CenterY=0 CenterZ=0 NormalX=0 NormalY=0 NormalZ=1 AngleXU=0 Radius=12
  constraints (2):
    c: Coincident(g0,g-1)
    c: Radius(g0) = 12
FEATURE [Part::Extrusion] Extrude045
  Base = -> Sketch055
  Dir = (0,0,1)
  DirMode = 2
  FaceMakerClass = Part::FaceMakerBullseye
  LengthFwd = 10
  LengthRev = 0
  Placement = pos=(0,0,-8.5) rot=(0,0,1;0rad)
  Solid = true
  Symmetric = false
FEATURE [Part::Fillet] Fillet
  Base = -> Extrude045
  Edges = 1 edges r=4: [Edge3]
FEATURE [Sketcher::SketchObject] Sketch056
  FullyConstrained = false
  sketch-geometry (1):
    g0: Circle CenterX=0 CenterY=0 CenterZ=0 NormalX=0 NormalY=0 NormalZ=1 AngleXU=0 Radius=4.5
  constraints (2):
    c: Coincident(g0,g-1)
    c: Radius(g0) = 4.5
FEATURE [Part::Extrusion] Extrude046
  Base = -> Sketch056
  Dir = (0,0,1)
  DirMode = 2
  FaceMakerClass = Part::FaceMakerBullseye
  LengthFwd = 10
  LengthRev = 0
  Solid = true
  Symmetric = false
FEATURE [Part::Cut] Cut
  Base = -> Fillet
  Tool = -> Extrude046
FEATURE [Part::Cut] Cut001
  Base = -> Cut
  Placement = pos=(65,-37,1.25) rot=(0,0,1;0rad)
  Tool = -> Extrude002
FEATURE [Part::Cut] Cut002
  Base = -> Cut
  Placement = pos=(65,35,1.25) rot=(0,0,1;0rad)
  Tool = -> Extrude002
FEATURE [Part::Cut] Cut003
  Base = -> Cut
  Placement = pos=(-37,32,1.25) rot=(0,0,1;0rad)
  Tool = -> Extrude002
FEATURE [Part::Cut] Cut004
  Base = -> Cut
  Placement = pos=(-40,-48,1.25) rot=(0,0,1;0rad)
  Tool = -> Extrude002
FEATURE [Part::Extrusion] Extrude047  label="Mutterloch001"
  Base = -> Sketch002
  Dir = (0,0,1)
  DirMode = 2
  FaceMakerClass = Part::FaceMakerBullseye
  LengthFwd = 8.5
  LengthRev = 0
  Placement = pos=(65,-37,1.25) rot=(0,0,1;0rad)
  Reversed = true
  Solid = true
  Symmetric = false
FEATURE [Part::Extrusion] Extrude048  label="Mutterloch002"
  Base = -> Sketch002
  Dir = (0,0,1)
  DirMode = 2
  FaceMakerClass = Part::FaceMakerBullseye
  LengthFwd = 8.5
  LengthRev = 0
  Placement = pos=(65,35,1.25) rot=(0,0,1;0rad)
  Reversed = true
  Solid = true
  Symmetric = false
FEATURE [Part::Extrusion] Extrude049  label="Mutterloch003"
  Base = -> Sketch002
  Dir = (0,0,1)
  DirMode = 2
  FaceMakerClass = Part::FaceMakerBullseye
  LengthFwd = 8.5
  LengthRev = 0
  Placement = pos=(-37,32,1.25) rot=(0,0,1;0rad)
  Reversed = true
  Solid = true
  Symmetric = false
FEATURE [Part::Extrusion] Extrude050  label="Mutterloch004"
  Base = -> Sketch002
  Dir = (0,0,1)
  DirMode = 2
  FaceMakerClass = Part::FaceMakerBullseye
  LengthFwd = 8.5
  LengthRev = 0
  Placement = pos=(-40,-48,1.25) rot=(0,0,1;0rad)
  Reversed = true
  Solid = true
  Symmetric = false
FEATURE [Part::MultiFuse] Fusion001
  Shapes = -> [Extrude050,Extrude049,Extrude048,Extrude047]
FEATURE [Part::Cut] Cut005
  Base = -> Extrude044
  Tool = -> Fusion001
FEATURE [Sketcher::SketchObject] Sketch033
  FullyConstrained = false
  Placement = pos=(0,0,0) rot=(1,0,0;3.14159rad)
  sketch-geometry (2):
    g0: Circle CenterX=-31.7644 CenterY=12.7082 CenterZ=0 NormalX=0 NormalY=0 NormalZ=1 AngleXU=0 Radius=2
    g1: Circle CenterX=-31.7644 CenterY=12.7082 CenterZ=0 NormalX=0 NormalY=0 NormalZ=1 AngleXU=0 Radius=9
  constraints (3):
    c: Coincident(g1,g0)
    c: Radius(g0) = 2
    c: Radius(g1) = 9
FEATURE [Part::Extrusion] Extrude029  label="Schalterbasis"
  Base = -> Sketch033
  Dir = (0,0,-1)
  DirMode = 2
  FaceMakerClass = Part::FaceMakerBullseye
  LengthFwd = 2
  LengthRev = 0
  Placement = pos=(0,0,-4) rot=(0,0,1;0rad)
  Solid = true
  Symmetric = false
FEATURE [Sketcher::SketchObject] Sketch057
  FullyConstrained = false
  Placement = pos=(0,0,0) rot=(1,0,0;3.14159rad)
  sketch-geometry (12):
    g0: Circle CenterX=-58.4659 CenterY=46.0837 CenterZ=0 NormalX=0 NormalY=0 NormalZ=1 AngleXU=0 Radius=1.5
    g1: Circle CenterX=-58.4659 CenterY=46.0837 CenterZ=0 NormalX=0 NormalY=0 NormalZ=1 AngleXU=0 Radius=2.64
    g2: Circle CenterX=-22.9147 CenterY=78.8059 CenterZ=0 NormalX=0 NormalY=0 NormalZ=1 AngleXU=0 Radius=1.5
    g3: Circle CenterX=-22.9147 CenterY=78.8059 CenterZ=0 NormalX=0 NormalY=0 NormalZ=1 AngleXU=0 Radius=2.64
    g4: Circle CenterX=19.8371 CenterY=57.8529 CenterZ=0 NormalX=0 NormalY=0 NormalZ=1 AngleXU=0 Radius=1.5
    g5: Circle CenterX=19.8371 CenterY=57.8529 CenterZ=0 NormalX=0 NormalY=0 NormalZ=1 AngleXU=0 Radius=2.64
    g6: Circle CenterX=74.9864 CenterY=-15.0107 CenterZ=0 NormalX=0 NormalY=0 NormalZ=1 AngleXU=0 Radius=1.5
    g7: Circle CenterX=74.9864 CenterY=-15.0107 CenterZ=0 NormalX=0 NormalY=0 NormalZ=1 AngleXU=0 Radius=2.64
    g8: Circle CenterX=22.6987 CenterY=-58.1327 CenterZ=0 NormalX=0 NormalY=0 NormalZ=1 AngleXU=0 Radius=1.5
    g9: Circle CenterX=22.6987 CenterY=-58.1327 CenterZ=0 NormalX=0 NormalY=0 NormalZ=1 AngleXU=0 Radius=2.64
    g10: Circle CenterX=-54.4678 CenterY=-45.841 CenterZ=0 NormalX=0 NormalY=0 NormalZ=1 AngleXU=0 Radius=1.5
    g11: Circle CenterX=-54.4678 CenterY=-45.841 CenterZ=0 NormalX=0 NormalY=0 NormalZ=1 AngleXU=0 Radius=2.64
  constraints (10):
    c: Radius(g0) = 1.5
    c: Coincident(g1,g0)
    c: Radius(g1) = 2.64
    c: Equal(g0,g2) = 1.5
    c: Coincident(g3,g2)
    c: Equal(g1,g3) = 2.64
    c: Coincident(g5,g4)
    c: Coincident(g7,g6)
    c: Coincident(g9,g8)
    c: Coincident(g11,g10)
FEATURE [Part::Extrusion] Extrude051
  Base = -> Sketch057
  Dir = (0,0,-1)
  DirMode = 2
  FaceMakerClass = Part::FaceMakerBullseye
  LengthFwd = 2
  LengthRev = 0
  Placement = pos=(0,0,-6) rot=(0,0,1;0rad)
  Solid = true
  Symmetric = false
FEATURE [Part::Cut] Cut006
  Base = -> Cut005
  Tool = -> Extrude051
FEATURE [Part::MultiFuse] Fusion
  Shapes = -> [Extrude,Extrude026,Extrude028,Cut001,Cut002,Cut003,Cut004,Extrude029,Cut006]
FEATURE [Part::Mirroring] Part__Mirroring  label="Fusion (Mirror #1)"
  Base = (0,0,0)
  Normal = (1,0,0)
  Source = -> Fusion
FEATURE [Mesh::Feature] left001  label="left"
FEATURE [Mesh::Feature] right
